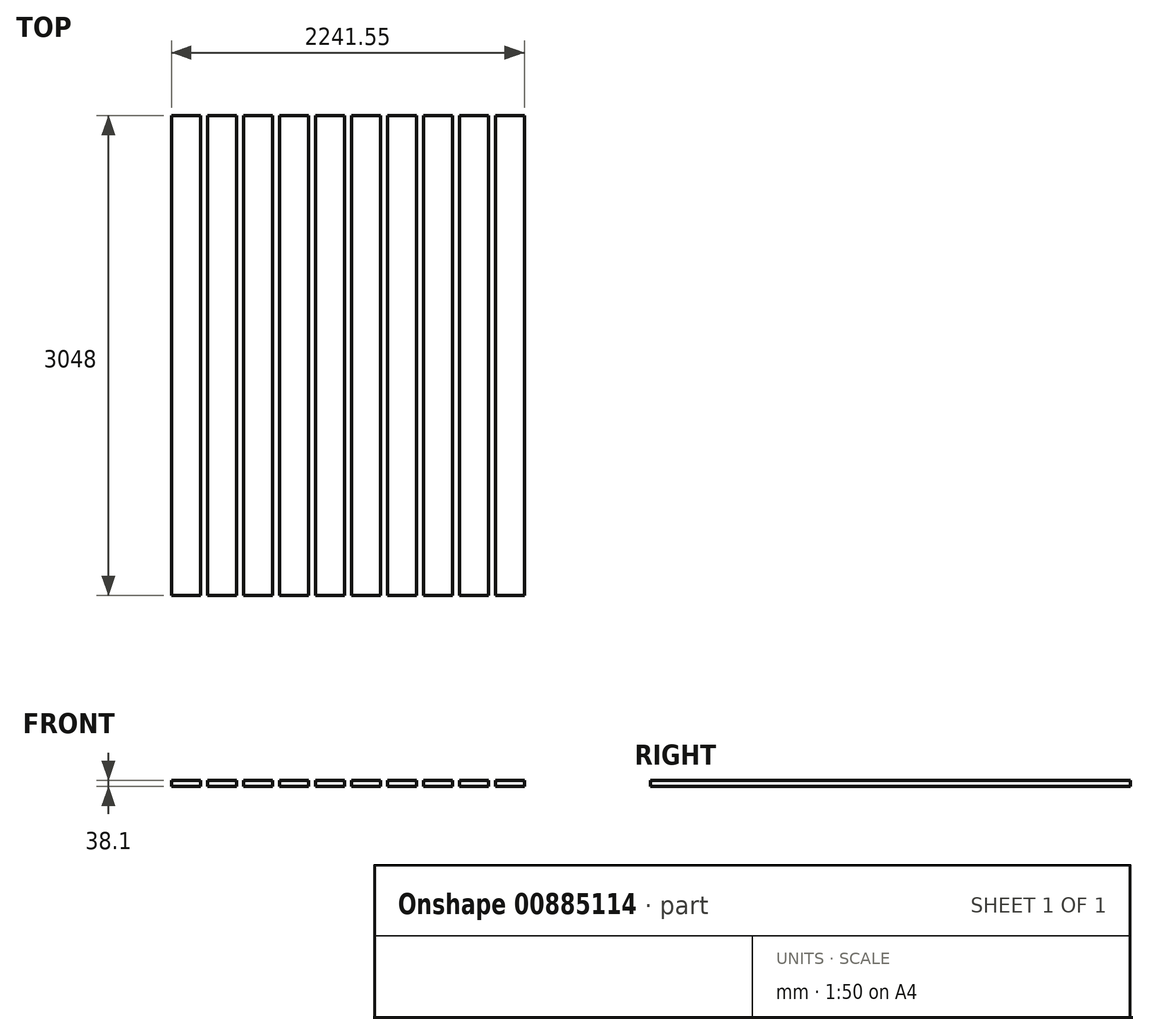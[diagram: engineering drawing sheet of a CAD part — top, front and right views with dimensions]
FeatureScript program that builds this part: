
annotation { "Feature Type Name" : "Feature", "Feature Type Description" : "" }
export const myFeature = defineFeature(function(context is Context, id is Id, definition is map)
    precondition{}
    {
        {
            var Q0;
            Q0=qCreatedBy(makeId("Front.planeOp"),FACE);
            var sketch = newSketch(context, id + "F0", { "sketchPlane" : qUnion([Q0])});
            skLineSegment(sketch, "E0.bottom", {"start": v(92.08, 19.05) * mm, "end": v(-92.08, 19.05) * mm});
            skLineSegment(sketch, "E0.top", {"start": v(92.08, -19.05) * mm, "end": v(-92.08, -19.05) * mm});
            skLineSegment(sketch, "E0.left", {"start": v(92.07, 19.05) * mm, "end": v(92.07, -19.05) * mm});
            skLineSegment(sketch, "E0.right", {"start": v(-92.08, 19.05) * mm, "end": v(-92.08, -19.05) * mm});
            skPoint(sketch, "E0.middle", {"position": v(0, 0) * mm});
            skLineSegment(sketch, "E1.1.0.0", {"start": v(320.68, 19.05) * mm, "end": v(320.68, -19.05) * mm});
            skLineSegment(sketch, "E1.1.0.1", {"start": v(136.53, 19.05) * mm, "end": v(136.53, -19.05) * mm});
            skLineSegment(sketch, "E1.1.0.2", {"start": v(320.68, 19.05) * mm, "end": v(136.53, 19.05) * mm});
            skPoint(sketch, "E1.1.0.3", {"position": v(228.6, 0) * mm});
            skLineSegment(sketch, "E1.1.0.4", {"start": v(320.68, -19.05) * mm, "end": v(136.53, -19.05) * mm});
            skLineSegment(sketch, "E1.2.0.0", {"start": v(549.27, 19.05) * mm, "end": v(549.27, -19.05) * mm});
            skLineSegment(sketch, "E1.2.0.1", {"start": v(365.13, 19.05) * mm, "end": v(365.13, -19.05) * mm});
            skLineSegment(sketch, "E1.2.0.2", {"start": v(549.28, 19.05) * mm, "end": v(365.13, 19.05) * mm});
            skPoint(sketch, "E1.2.0.3", {"position": v(457.2, 0) * mm});
            skLineSegment(sketch, "E1.2.0.4", {"start": v(549.28, -19.05) * mm, "end": v(365.13, -19.05) * mm});
            skLineSegment(sketch, "E1.3.0.0", {"start": v(777.88, 19.05) * mm, "end": v(777.88, -19.05) * mm});
            skLineSegment(sketch, "E1.3.0.1", {"start": v(593.73, 19.05) * mm, "end": v(593.73, -19.05) * mm});
            skLineSegment(sketch, "E1.3.0.2", {"start": v(777.88, 19.05) * mm, "end": v(593.73, 19.05) * mm});
            skPoint(sketch, "E1.3.0.3", {"position": v(685.8, 0) * mm});
            skLineSegment(sketch, "E1.3.0.4", {"start": v(777.88, -19.05) * mm, "end": v(593.73, -19.05) * mm});
            skLineSegment(sketch, "E1.4.0.0", {"start": v(1006.48, 19.05) * mm, "end": v(1006.48, -19.05) * mm});
            skLineSegment(sketch, "E1.4.0.1", {"start": v(822.33, 19.05) * mm, "end": v(822.33, -19.05) * mm});
            skLineSegment(sketch, "E1.4.0.2", {"start": v(1006.48, 19.05) * mm, "end": v(822.33, 19.05) * mm});
            skPoint(sketch, "E1.4.0.3", {"position": v(914.4, 0) * mm});
            skLineSegment(sketch, "E1.4.0.4", {"start": v(1006.48, -19.05) * mm, "end": v(822.33, -19.05) * mm});
            skLineSegment(sketch, "E1.5.0.0", {"start": v(1235.08, 19.05) * mm, "end": v(1235.08, -19.05) * mm});
            skLineSegment(sketch, "E1.5.0.1", {"start": v(1050.93, 19.05) * mm, "end": v(1050.93, -19.05) * mm});
            skLineSegment(sketch, "E1.5.0.2", {"start": v(1235.08, 19.05) * mm, "end": v(1050.93, 19.05) * mm});
            skPoint(sketch, "E1.5.0.3", {"position": v(1143, 0) * mm});
            skLineSegment(sketch, "E1.5.0.4", {"start": v(1235.08, -19.05) * mm, "end": v(1050.93, -19.05) * mm});
            skLineSegment(sketch, "E1.6.0.0", {"start": v(1463.67, 19.05) * mm, "end": v(1463.67, -19.05) * mm});
            skLineSegment(sketch, "E1.6.0.1", {"start": v(1279.53, 19.05) * mm, "end": v(1279.53, -19.05) * mm});
            skLineSegment(sketch, "E1.6.0.2", {"start": v(1463.68, 19.05) * mm, "end": v(1279.53, 19.05) * mm});
            skPoint(sketch, "E1.6.0.3", {"position": v(1371.6, 0) * mm});
            skLineSegment(sketch, "E1.6.0.4", {"start": v(1463.68, -19.05) * mm, "end": v(1279.53, -19.05) * mm});
            skLineSegment(sketch, "E1.7.0.0", {"start": v(1692.27, 19.05) * mm, "end": v(1692.27, -19.05) * mm});
            skLineSegment(sketch, "E1.7.0.1", {"start": v(1508.13, 19.05) * mm, "end": v(1508.13, -19.05) * mm});
            skLineSegment(sketch, "E1.7.0.2", {"start": v(1692.28, 19.05) * mm, "end": v(1508.13, 19.05) * mm});
            skPoint(sketch, "E1.7.0.3", {"position": v(1600.2, 0) * mm});
            skLineSegment(sketch, "E1.7.0.4", {"start": v(1692.28, -19.05) * mm, "end": v(1508.13, -19.05) * mm});
            skLineSegment(sketch, "E1.8.0.0", {"start": v(1920.88, 19.05) * mm, "end": v(1920.88, -19.05) * mm});
            skLineSegment(sketch, "E1.8.0.1", {"start": v(1736.73, 19.05) * mm, "end": v(1736.73, -19.05) * mm});
            skLineSegment(sketch, "E1.8.0.2", {"start": v(1920.88, 19.05) * mm, "end": v(1736.73, 19.05) * mm});
            skPoint(sketch, "E1.8.0.3", {"position": v(1828.8, 0) * mm});
            skLineSegment(sketch, "E1.8.0.4", {"start": v(1920.88, -19.05) * mm, "end": v(1736.73, -19.05) * mm});
            skLineSegment(sketch, "E1.9.0.0", {"start": v(2149.48, 19.05) * mm, "end": v(2149.48, -19.05) * mm});
            skLineSegment(sketch, "E1.9.0.1", {"start": v(1965.33, 19.05) * mm, "end": v(1965.33, -19.05) * mm});
            skLineSegment(sketch, "E1.9.0.2", {"start": v(2149.48, 19.05) * mm, "end": v(1965.33, 19.05) * mm});
            skPoint(sketch, "E1.9.0.3", {"position": v(2057.4, 0) * mm});
            skLineSegment(sketch, "E1.9.0.4", {"start": v(2149.48, -19.05) * mm, "end": v(1965.33, -19.05) * mm});
            skLineSegment(sketch, "E1.direction1", {"start": v(-92.08, -19.05) * mm, "end": v(136.53, -19.05) * mm, "construction": true});
            skSolve(sketch);
        }
        {
            var Q0;
            Q0=makeQuery(id+"F0.imprint","IMPRINT",FACE,{"disambiguationData":[TD([[makeQuery(id+"F0.imprint","IMPRINT",EDGE,{"derivedFrom":sQuery(id+"F0.wireOp",EDGE,"E1.1.0.0")}),-1.0]])]});
            var Q1;
            Q1=makeQuery(id+"F0.imprint","IMPRINT",FACE,{"disambiguationData":[TD([[makeQuery(id+"F0.imprint","IMPRINT",EDGE,{"derivedFrom":sQuery(id+"F0.wireOp",EDGE,"E1.2.0.0")}),-1.0]])]});
            var Q2;
            Q2=makeQuery(id+"F0.imprint","IMPRINT",FACE,{"disambiguationData":[TD([[makeQuery(id+"F0.imprint","IMPRINT",EDGE,{"derivedFrom":sQuery(id+"F0.wireOp",EDGE,"E1.3.0.0")}),-1.0]])]});
            var Q3;
            Q3=makeQuery(id+"F0.imprint","IMPRINT",FACE,{"disambiguationData":[TD([[makeQuery(id+"F0.imprint","IMPRINT",EDGE,{"derivedFrom":sQuery(id+"F0.wireOp",EDGE,"E1.4.0.0")}),-1.0]])]});
            var Q4;
            Q4=makeQuery(id+"F0.imprint","IMPRINT",FACE,{"disambiguationData":[TD([[makeQuery(id+"F0.imprint","IMPRINT",EDGE,{"derivedFrom":sQuery(id+"F0.wireOp",EDGE,"E1.5.0.0")}),-1.0]])]});
            var Q5;
            Q5=makeQuery(id+"F0.imprint","IMPRINT",FACE,{"disambiguationData":[TD([[makeQuery(id+"F0.imprint","IMPRINT",EDGE,{"derivedFrom":sQuery(id+"F0.wireOp",EDGE,"E1.6.0.0")}),-1.0]])]});
            var Q6;
            Q6=makeQuery(id+"F0.imprint","IMPRINT",FACE,{"disambiguationData":[TD([[makeQuery(id+"F0.imprint","IMPRINT",EDGE,{"derivedFrom":sQuery(id+"F0.wireOp",EDGE,"E1.7.0.0")}),-1.0]])]});
            var Q7;
            Q7=makeQuery(id+"F0.imprint","IMPRINT",FACE,{"disambiguationData":[TD([[makeQuery(id+"F0.imprint","IMPRINT",EDGE,{"derivedFrom":sQuery(id+"F0.wireOp",EDGE,"E1.8.0.0")}),-1.0]])]});
            var Q8;
            Q8=makeQuery(id+"F0.imprint","IMPRINT",FACE,{"disambiguationData":[TD([[makeQuery(id+"F0.imprint","IMPRINT",EDGE,{"derivedFrom":sQuery(id+"F0.wireOp",EDGE,"E1.9.0.0")}),-1.0]])]});
            var Q9;
            Q9=makeQuery(id+"F0.imprint","IMPRINT",FACE,{"disambiguationData":[TD([[makeQuery(id+"F0.imprint","IMPRINT",EDGE,{"derivedFrom":sQuery(id+"F0.wireOp",EDGE,"E0.bottom")}),1.0]])]});
            extrude(context, id + "F1", {"entities" : qUnion([Q0, Q1, Q2, Q3, Q4, Q5, Q6, Q7, Q8, Q9]), "depth" : 3048 * mm, "offsetDistance" : 25.4 * mm});
        }
    });
